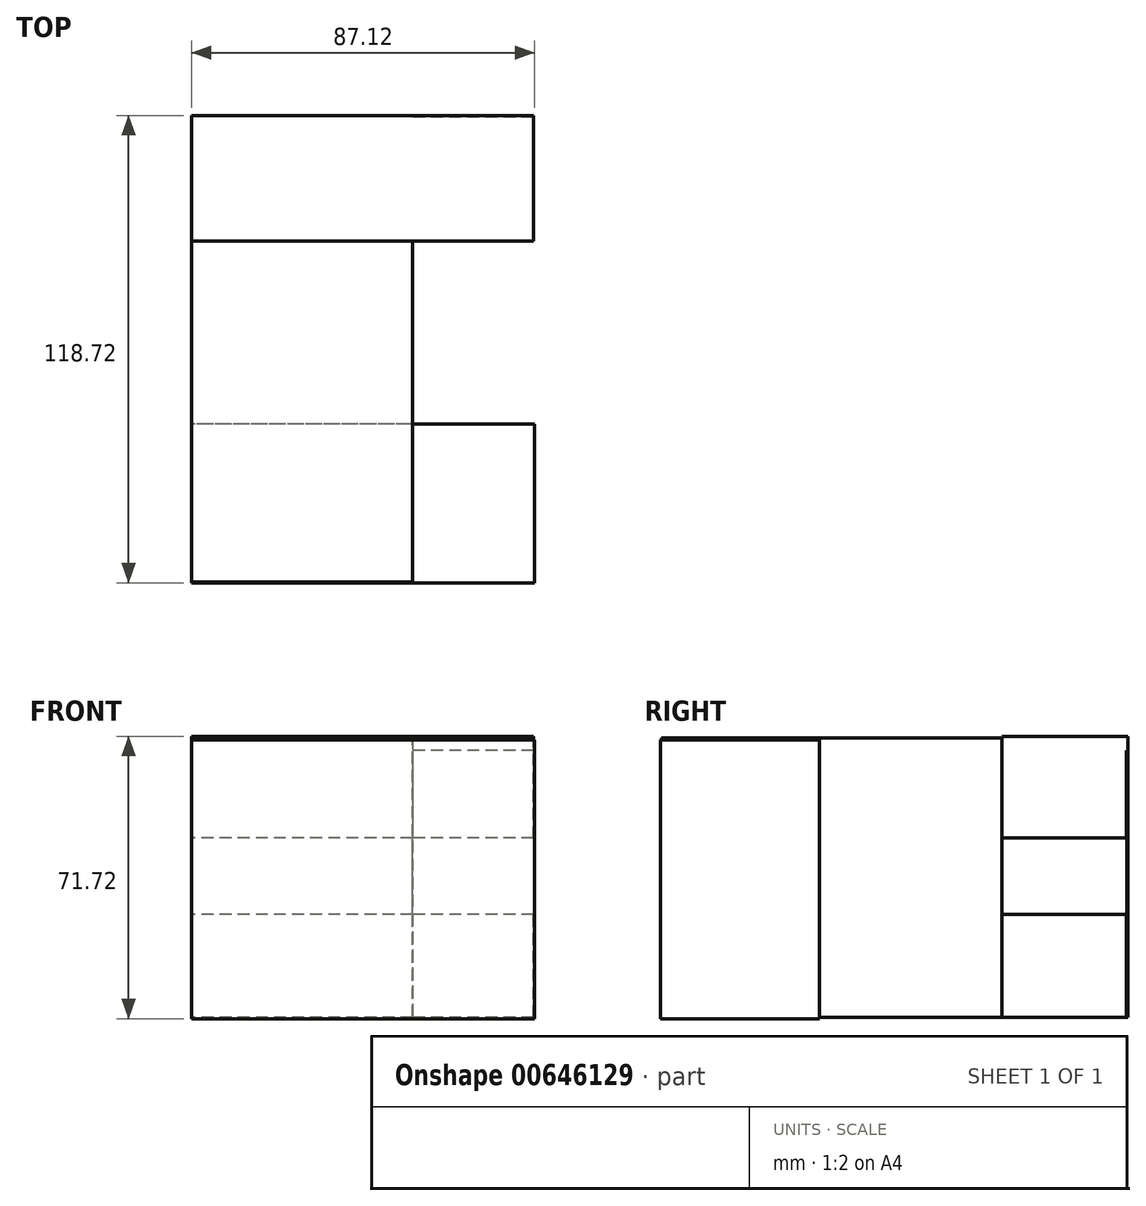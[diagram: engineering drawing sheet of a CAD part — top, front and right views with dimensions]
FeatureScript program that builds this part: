
annotation { "Feature Type Name" : "Feature", "Feature Type Description" : "" }
export const myFeature = defineFeature(function(context is Context, id is Id, definition is map)
    precondition{}
    {
        {
            var Q0;
            Q0=qCreatedBy(makeId("Right.planeOp"),FACE);
            var sketch = newSketch(context, id + "F0", { "sketchPlane" : qUnion([Q0])});
            skLineSegment(sketch, "E0.bottom", {"start": v(-86.6, 15.95) * mm, "end": v(31.93, 15.95) * mm});
            skLineSegment(sketch, "E0.top", {"start": v(-86.6, -55.03) * mm, "end": v(31.93, -55.03) * mm});
            skLineSegment(sketch, "E0.left", {"start": v(-86.6, 15.95) * mm, "end": v(-86.6, -55.03) * mm});
            skLineSegment(sketch, "E0.right", {"start": v(31.93, 15.95) * mm, "end": v(31.93, -55.03) * mm});
            skSolve(sketch);
        }
        {
            var Q0;
            Q0 = qSketchRegion(id + "F0", true);
            extrude(context, id + "F1", {"entities" : qUnion([Q0]), "depth" : 56.13 * mm, "offsetDistance" : 25.4 * mm});
        }
        {
            var Q0;
            Q0=qCreatedBy(makeId("Right.planeOp"),FACE);
            var sketch = newSketch(context, id + "F2", { "sketchPlane" : qUnion([Q0])});
            skLineSegment(sketch, "E1.bottom", {"start": v(-86.8, 15.4) * mm, "end": v(-46.42, 15.4) * mm});
            skLineSegment(sketch, "E1.top", {"start": v(-86.8, -55.4) * mm, "end": v(-46.42, -55.4) * mm});
            skLineSegment(sketch, "E1.left", {"start": v(-86.8, 15.4) * mm, "end": v(-86.8, -55.4) * mm});
            skLineSegment(sketch, "E1.right", {"start": v(-46.42, 15.4) * mm, "end": v(-46.42, -55.4) * mm});
            skSolve(sketch);
        }
        {
            var Q0;
            Q0 = qSketchRegion(id + "F2", true);
            extrude(context, id + "F3", {"entities" : qUnion([Q0]), "operationType" : NewBodyOperationType.ADD, "depth" : 87.12 * mm, "offsetDistance" : 25.4 * mm});
        }
        {
            var Q0;
            Q0=qCreatedBy(makeId("Right.planeOp"),FACE);
            var sketch = newSketch(context, id + "F4", { "sketchPlane" : qUnion([Q0])});
            skLineSegment(sketch, "E2.bottom", {"start": v(0, 16.32) * mm, "end": v(31.93, 16.32) * mm});
            skLineSegment(sketch, "E2.top", {"start": v(0, 12.81) * mm, "end": v(31.93, 12.81) * mm});
            skLineSegment(sketch, "E2.left", {"start": v(0, 16.32) * mm, "end": v(0, 12.81) * mm});
            skLineSegment(sketch, "E2.right", {"start": v(31.93, 16.32) * mm, "end": v(31.93, 12.81) * mm});
            skLineSegment(sketch, "E3.bottom", {"start": v(31.57, -55.03) * mm, "end": v(0, -55.03) * mm});
            skLineSegment(sketch, "E3.top", {"start": v(31.57, 16.32) * mm, "end": v(0, 16.32) * mm});
            skLineSegment(sketch, "E3.left", {"start": v(31.57, -55.03) * mm, "end": v(31.57, 16.32) * mm});
            skLineSegment(sketch, "E3.right", {"start": v(0, -55.03) * mm, "end": v(0, 16.32) * mm});
            skSolve(sketch);
        }
        {
            var Q0;
            Q0 = qSketchRegion(id + "F4", true);
            extrude(context, id + "F5", {"entities" : qUnion([Q0]), "operationType" : NewBodyOperationType.ADD, "depth" : 86.87 * mm, "offsetDistance" : 25.4 * mm});
        }
        {
            var Q0;
            Q0=qCreatedBy(makeId("Right.planeOp"),FACE);
            var sketch = newSketch(context, id + "F6", { "sketchPlane" : qUnion([Q0])});
            skLineSegment(sketch, "E4.bottom", {"start": v(0, -9.5) * mm, "end": v(31.75, -9.5) * mm});
            skLineSegment(sketch, "E4.top", {"start": v(0, -28.85) * mm, "end": v(31.75, -28.85) * mm});
            skLineSegment(sketch, "E4.left", {"start": v(0, -9.5) * mm, "end": v(0, -28.85) * mm});
            skLineSegment(sketch, "E4.right", {"start": v(31.75, -9.5) * mm, "end": v(31.75, -28.85) * mm});
            skSolve(sketch);
        }
        {
            var Q0;
            Q0 = qSketchRegion(id + "F6", true);
            extrude(context, id + "F7", {"entities" : qUnion([Q0]), "operationType" : NewBodyOperationType.REMOVE, "depth" : 92.7 * mm, "offsetDistance" : 25.4 * mm});
        }
    });
